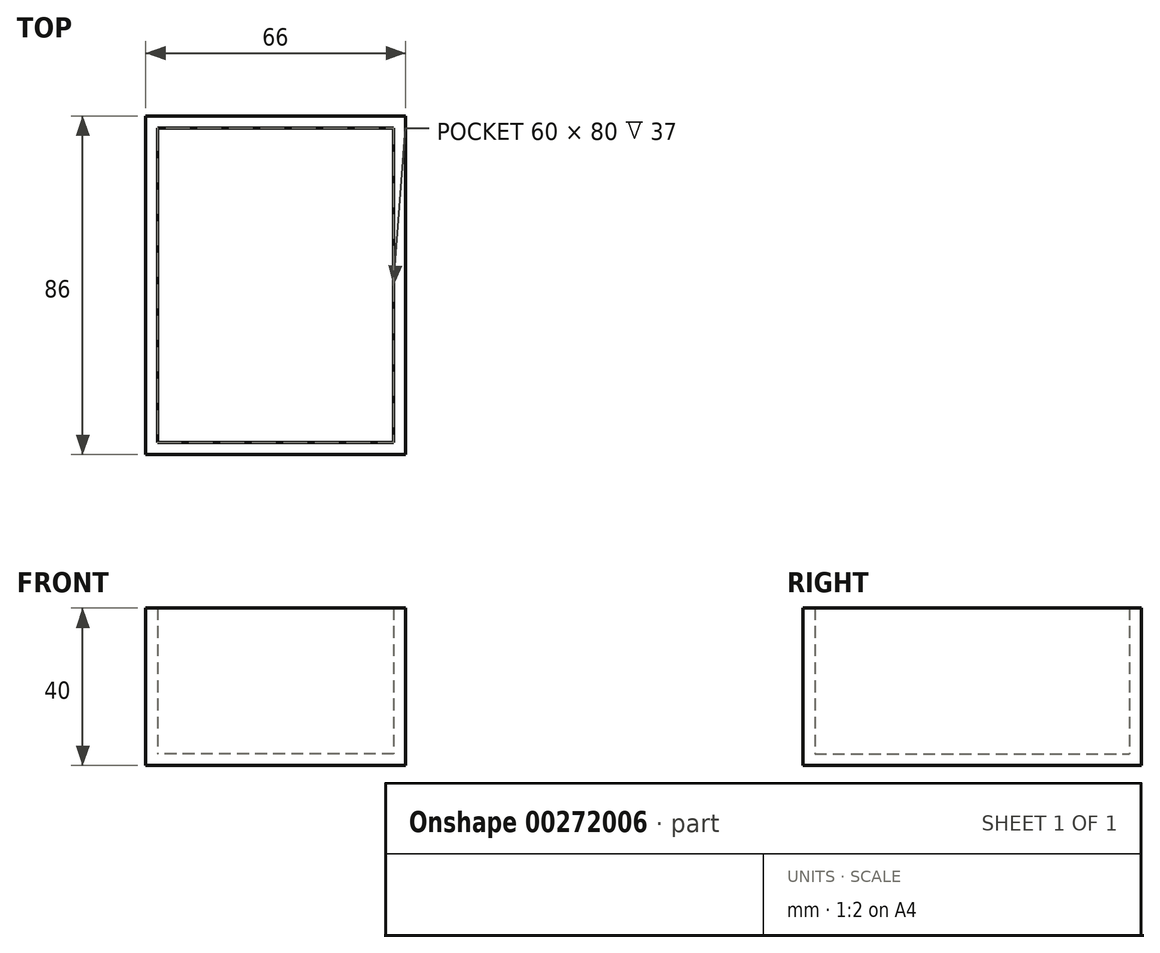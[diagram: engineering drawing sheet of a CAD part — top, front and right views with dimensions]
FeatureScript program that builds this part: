
annotation { "Feature Type Name" : "Feature", "Feature Type Description" : "" }
export const myFeature = defineFeature(function(context is Context, id is Id, definition is map)
    precondition{}
    {
        {
            var Q0;
            Q0=qCreatedBy(makeId("Top.planeOp"),FACE);
            var sketch = newSketch(context, id + "F0", { "sketchPlane" : qUnion([Q0])});
            skLineSegment(sketch, "E0.bottom", {"start": v(-33, 43) * mm, "end": v(33, 43) * mm});
            skLineSegment(sketch, "E0.top", {"start": v(-33, -43) * mm, "end": v(33, -43) * mm});
            skLineSegment(sketch, "E0.left", {"start": v(-33, 43) * mm, "end": v(-33, -43) * mm});
            skLineSegment(sketch, "E0.right", {"start": v(33, 43) * mm, "end": v(33, -43) * mm});
            skLineSegment(sketch, "E1.bottom", {"start": v(-30, 40) * mm, "end": v(30, 40) * mm});
            skLineSegment(sketch, "E1.top", {"start": v(-30, -40) * mm, "end": v(30, -40) * mm});
            skLineSegment(sketch, "E1.left", {"start": v(-30, 40) * mm, "end": v(-30, -40) * mm});
            skLineSegment(sketch, "E1.right", {"start": v(30, 40) * mm, "end": v(30, -40) * mm});
            skLineSegment(sketch, "E2", {"start": v(-30, -40) * mm, "end": v(30, 40) * mm, "construction": true});
            skLineSegment(sketch, "E3", {"start": v(30, 40) * mm, "end": v(33, 40) * mm, "construction": true});
            skLineSegment(sketch, "E4", {"start": v(-30, 40) * mm, "end": v(-30, 43) * mm, "construction": true});
            skLineSegment(sketch, "E5", {"start": v(-30, -40) * mm, "end": v(-33, -40) * mm, "construction": true});
            skLineSegment(sketch, "E6", {"start": v(30, -40) * mm, "end": v(30, -43) * mm, "construction": true});
            skSolve(sketch);
        }
        {
            var Q0;
            Q0=makeQuery(id+"F0.imprint","IMPRINT",FACE,{"disambiguationData":[TD([[makeQuery(id+"F0.imprint","IMPRINT",EDGE,{"derivedFrom":sQuery(id+"F0.wireOp",EDGE,"E0.bottom")}),-1.0]])]});
            var Q1;
            Q1=makeQuery(id+"F0.imprint","IMPRINT",FACE,{"disambiguationData":[TD([[makeQuery(id+"F0.imprint","IMPRINT",EDGE,{"derivedFrom":sQuery(id+"F0.wireOp",EDGE,"E1.bottom")}),-1.0]])]});
            extrude(context, id + "F1", {"entities" : qUnion([Q0, Q1]), "depth" : 3 * mm});
        }
        {
            var Q0;
            Q0 = qSketchRegion(id + "F0", true);
            extrude(context, id + "F2", {"entities" : qUnion([Q0]), "operationType" : NewBodyOperationType.ADD, "depth" : 40 * mm});
        }
    });
